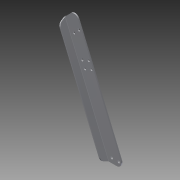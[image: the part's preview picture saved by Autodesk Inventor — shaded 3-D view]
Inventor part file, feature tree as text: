
AUTODESK INVENTOR PART (.ipt)
format: ipt  version: 2014 SP1 (Build 180222100, 222)  size: 253,952 bytes
history: native  units: in
note: dims shown in document units (in); Inventor stores cm internally (conversion verified against a paired STEP export)
features: reference x5, sheet_metal_op x2, other x2, sketch x1, chamfer x1
ambient origin geometry x8: Origin, YZ Plane, XZ Plane, XY Plane, X Axis, Y Axis, Z Axis, Center Point
bodies: Solid1 (feature_tree)
feature tree (11):
  sketch  "Sketch1"  dims[d1=0.5in d2=1.0in d3=0.5in d4=0.75in d5=0.125in d6=0.125in d7=0.0625in d8=0.25in d9=0.125in d10=90.0deg d11=0.05in d12=0.5in d16=0.266in d17=0.7874in d19=0.75in d20=0.7874in d22=0.75in d25=0.75in d26=2.25in d27=0.5in d28=0.1in d29=0.5in d30=12.0831in d31=3.937in d33=1.1759in d34=0.3937in d36=1.0in d38=0.5in d39=0.75in d40=0.875in d41=2.5in d42=12.7044in d43=3.1496in d45=1.2841in d46=0.3937in d48=1.0in]
  sheet_metal_op  "Face1"
  sheet_metal_op  "Fold1"
  chamfer  "Corner Round1"
  reference  "Reference1"
  reference  "Reference2"
  other  "Plate1"
  reference  "Reference15"
  reference  "Reference16"
  reference  "Reference17"
  other  "Definition1"
